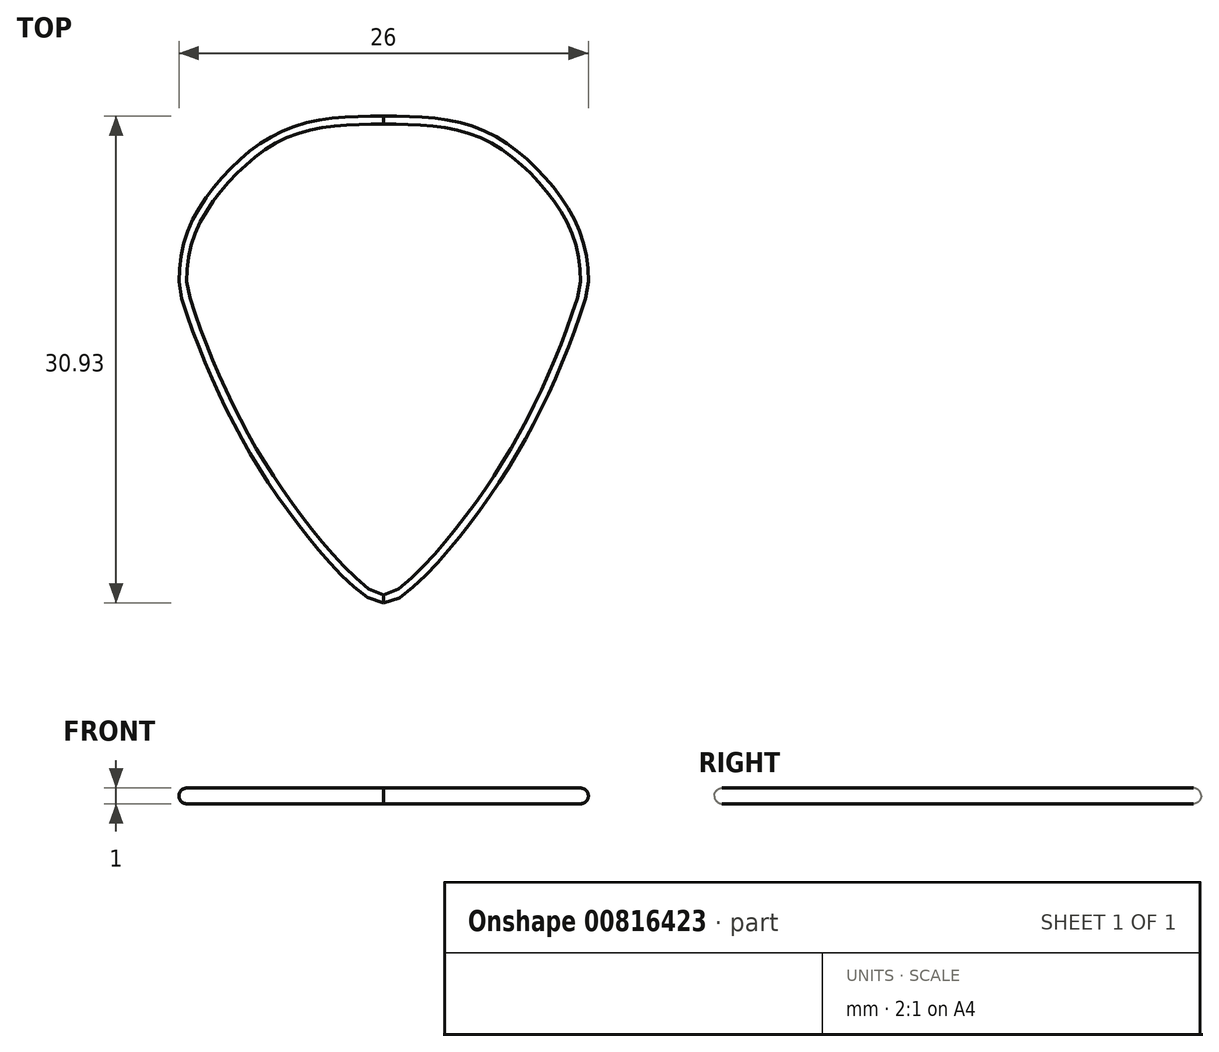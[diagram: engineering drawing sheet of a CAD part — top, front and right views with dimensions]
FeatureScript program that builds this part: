
annotation { "Feature Type Name" : "Feature", "Feature Type Description" : "" }
export const myFeature = defineFeature(function(context is Context, id is Id, definition is map)
    precondition{}
    {
        {
            var Q0;
            Q0=qCreatedBy(makeId("Top.planeOp"),FACE);
            var sketch = newSketch(context, id + "F0", { "sketchPlane" : qUnion([Q0])});
            skLineSegment(sketch, "E0.bottom", {"start": v(0, 0) * mm, "end": v(-26, 0) * mm});
            skLineSegment(sketch, "E0.top", {"start": v(0, 32) * mm, "end": v(-26, 32) * mm});
            skLineSegment(sketch, "E0.left", {"start": v(0, 0) * mm, "end": v(0, 32) * mm});
            skLineSegment(sketch, "E0.right", {"start": v(-26, 0) * mm, "end": v(-26, 32) * mm});
            skLineSegment(sketch, "E1", {"start": v(-13, 32) * mm, "end": v(-13, 0) * mm});
            skPoint(sketch, "E2", {"position": v(-13, 21) * mm});
            skLineSegment(sketch, "E3", {"start": v(-13, 21) * mm, "end": v(-26, 21) * mm});
            skLineSegment(sketch, "E4", {"start": v(-26, 21) * mm, "end": v(0, 21) * mm});
            skFitSpline(sketch, "E5", {"points": [v(-26, 21) * mm, v(-24.42, 26.13) * mm, v(-19.48, 30.55) * mm, v(-13, 31.52) * mm], "startDerivative": vector(0, 20.14) * mm, "endDerivative": vector(20.6, 0.17) * mm});
            skFitSpline(sketch, "E6", {"points": [v(-26, 21) * mm, v(-25.91, 20.29) * mm, v(-21.67, 10.42) * mm, v(-14.1, 0.99) * mm, v(-13, 0.59) * mm], "startDerivative": vector(0, -8.51) * mm, "endDerivative": vector(7.43, -0.85) * mm});
            skFitSpline(sketch, "E7.MirrorCS", {"points": [v(0, 21) * mm, v(-1.58, 26.13) * mm, v(-6.52, 30.55) * mm, v(-13, 31.52) * mm], "startDerivative": vector(0, 20.14) * mm, "endDerivative": vector(-20.6, 0.17) * mm});
            skFitSpline(sketch, "E8.MirrorCS", {"points": [v(0, 21) * mm, v(-0.09, 20.29) * mm, v(-4.33, 10.42) * mm, v(-11.9, 0.99) * mm, v(-13, 0.59) * mm], "startDerivative": vector(0, -8.51) * mm, "endDerivative": vector(-7.43, -0.85) * mm});
            skSolve(sketch);
        }
        {
            var Q0;
            {var subQ0=sQuery(id+"F0.wireOp",EDGE,"E5");Q0=makeQuery(id+"F0.imprint","IMPRINT",FACE,{"disambiguationData":[TD([[makeQuery(id+"F0.imprint","IMPRINT",EDGE,{"derivedFrom":subQ0}),-1.0]])]});}
            var Q1;
            {var subQ0=sQuery(id+"F0.wireOp",EDGE,"E7.MirrorCS");Q1=makeQuery(id+"F0.imprint","IMPRINT",FACE,{"disambiguationData":[TD([[makeQuery(id+"F0.imprint","IMPRINT",EDGE,{"derivedFrom":subQ0}),1.0]])]});}
            var Q2;
            {var subQ0=sQuery(id+"F0.wireOp",EDGE,"E6");Q2=makeQuery(id+"F0.imprint","IMPRINT",FACE,{"disambiguationData":[TD([[makeQuery(id+"F0.imprint","IMPRINT",EDGE,{"derivedFrom":subQ0}),1.0]])]});}
            var Q3;
            {var subQ0=sQuery(id+"F0.wireOp",EDGE,"E8.MirrorCS");Q3=makeQuery(id+"F0.imprint","IMPRINT",FACE,{"disambiguationData":[TD([[makeQuery(id+"F0.imprint","IMPRINT",EDGE,{"derivedFrom":subQ0}),-1.0]])]});}
            extrude(context, id + "F1", {"entities" : qUnion([Q0, Q1, Q2, Q3]), "depth" : 1 * mm, "offsetDistance" : 25 * mm});
        }
        {
            var Q0;
            Q0=makeQuery(id+"F1.opExtrude","CAP_EDGE",EDGE,{"disambiguationData":[OSD([sQuery(id+"F0.wireOp",EDGE,"E6")])],"isStart":false});
            var Q1;
            Q1=makeQuery(id+"F1.opExtrude","CAP_EDGE",EDGE,{"disambiguationData":[OSD([sQuery(id+"F0.wireOp",EDGE,"E8.MirrorCS")])],"isStart":false});
            var Q2;
            Q2=makeQuery(id+"F1.opExtrude","CAP_EDGE",EDGE,{"disambiguationData":[OSD([sQuery(id+"F0.wireOp",EDGE,"E6")])],"isStart":true});
            var Q3;
            Q3=makeQuery(id+"F1.opExtrude","CAP_EDGE",EDGE,{"disambiguationData":[OSD([sQuery(id+"F0.wireOp",EDGE,"E8.MirrorCS")])],"isStart":true});
            fillet(context, id + "F2", {"entities" : qUnion([Q0, Q1, Q2, Q3]), "radius" : 0.5 * mm, "tangentPropagation" : true, "allowEdgeOverflow" : false});
        }
    });
